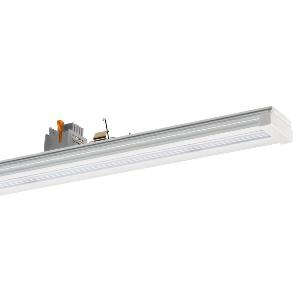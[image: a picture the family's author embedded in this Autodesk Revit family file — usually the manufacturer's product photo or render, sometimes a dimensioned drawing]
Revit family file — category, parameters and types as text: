
# Revit family: conveo_-_cvg_8000_840_xn-p_da_7_226848159-00804953_a6d2
name_source: partatom
category: Lighting Fixtures
units: mm (PartAtom-declared; Revit-internal decimal feet)

## family parameters
Cut with Voids When Loaded = No
Host = Face
Light Source = No
Part Type = Normal
Room Calculation Point = No
Round Connector Dimension = Use Diameter
Shared = No

## types (1)
- CONVEO - CVG 8000/840/xN-P/DA/7 (1 x LED, 7600 lm, 4000K)
    Apparent Load = 55 VA
    Approval mark = CE
    CIE Flux Codes = 57 84 97 100 100
    Color Rendering = 80-89
    Color Temperature = 4000K
    Control Gear = Electronic ballast
    Default Elevation = 1800 mm
    Description = CVG 8000/840/xN-P/DA/7|Continuous-row system|light source: LED|work equipment: Adjustable electronic ballast, digital DALI|connected load: 220-240 V, 50-60 Hz|Power consumption: approx. 55 W|luminous flux: 7600 lm|luminous efficacy: 138 lm/W|colour temperature: Cold white, ca. 4000 K|color rendering index (CRI): >= 80|chromaticity tolerance:  3 SDCM|System of protection: IP 54|class of protection: I|technology: Continuously dimmable|luminaire body|material: Aluminium|surface: Powder coatet|colour: White|lamp cover: Acrylic (PMMA), Satine|weight (net): approx. 1.9 kg|Fastening: Available separately|minimum ambient temperature: -25 ░C|maximum ambient temperature: 45 ░C|glare control: Prism optics (linear)|Approval mark: VDE - ENEC|
    Frequency = 50 Hz
    Height = 70 mm
    Lamp = 1 x LED
    Lamp Light Flux = 7600 lm
    Lamp count = 1
    Length = 1500 mm
    Luminous efficacy = 138 lm/W
    Manufacturer = Waldmann
    ModVariant = No
    Model = 226848159-00804953
    Mounting Place = Ceiling
    Mounting Type = Pendant
    Number of Poles = 1
    OnlyDefault = Yes
    Power Factor = 1
    Product Name = CONVEO - CVG 8000/840/xN-P/DA/7
    Product group = Continuous-row system (industry)
    ProductGroupID = 301
    Protection Class = Protection class I
    Protection Degree = IP 54
    RLX_Detail_Level = 1
    RlxData = <blob elided: 99921 chars, md5=5487a959>
    Socket = socket
    Standby Power = 0 W
    System Light Flux = 7600 lm
    System Power = 55 W
    Type Comments = Product without accessories
    Type Image = 226848019-00804937-1p7.jpg
    URL = http://relux.com
    VarID = ---
    Voltage = 230 V
    Voltage Range = 220-240 V
    Weight = 0.00 kg
    Width = 64 mm

## geometry (parser evidence)
native form markers: Blend x4, Sweep x9
no freeform markers — native parametric forms only
